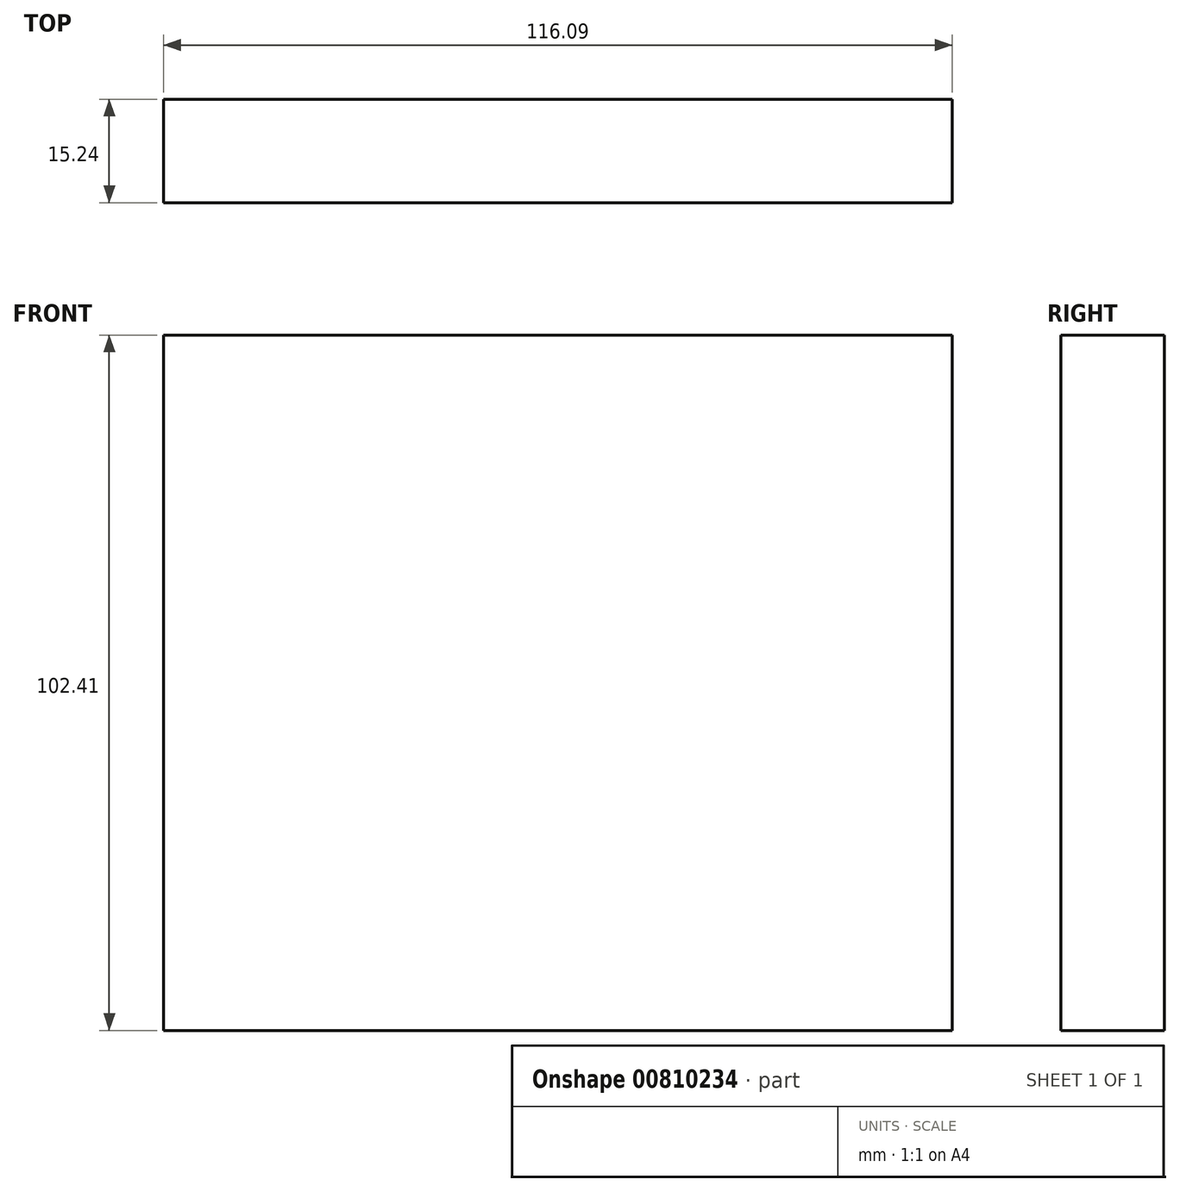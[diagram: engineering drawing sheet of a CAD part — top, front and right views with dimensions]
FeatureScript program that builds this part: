
annotation { "Feature Type Name" : "Feature", "Feature Type Description" : "" }
export const myFeature = defineFeature(function(context is Context, id is Id, definition is map)
    precondition{}
    {
        {
            var Q0;
            Q0=qCreatedBy(makeId("Front.planeOp"),FACE);
            var sketch = newSketch(context, id + "F0", { "sketchPlane" : qUnion([Q0])});
            skLineSegment(sketch, "E0.bottom", {"start": v(-56.5, 47.23) * mm, "end": v(59.6, 47.23) * mm});
            skLineSegment(sketch, "E0.top", {"start": v(-56.5, -55.18) * mm, "end": v(59.6, -55.18) * mm});
            skLineSegment(sketch, "E0.left", {"start": v(-56.5, 47.23) * mm, "end": v(-56.5, -55.18) * mm});
            skLineSegment(sketch, "E0.right", {"start": v(59.6, 47.23) * mm, "end": v(59.6, -55.18) * mm});
            skSolve(sketch);
        }
        {
            var Q0;
            Q0 = qSketchRegion(id + "F0", true);
            extrude(context, id + "F1", {"entities" : qUnion([Q0]), "depth" : 15.24 * mm, "offsetDistance" : 25.4 * mm});
        }
    });
